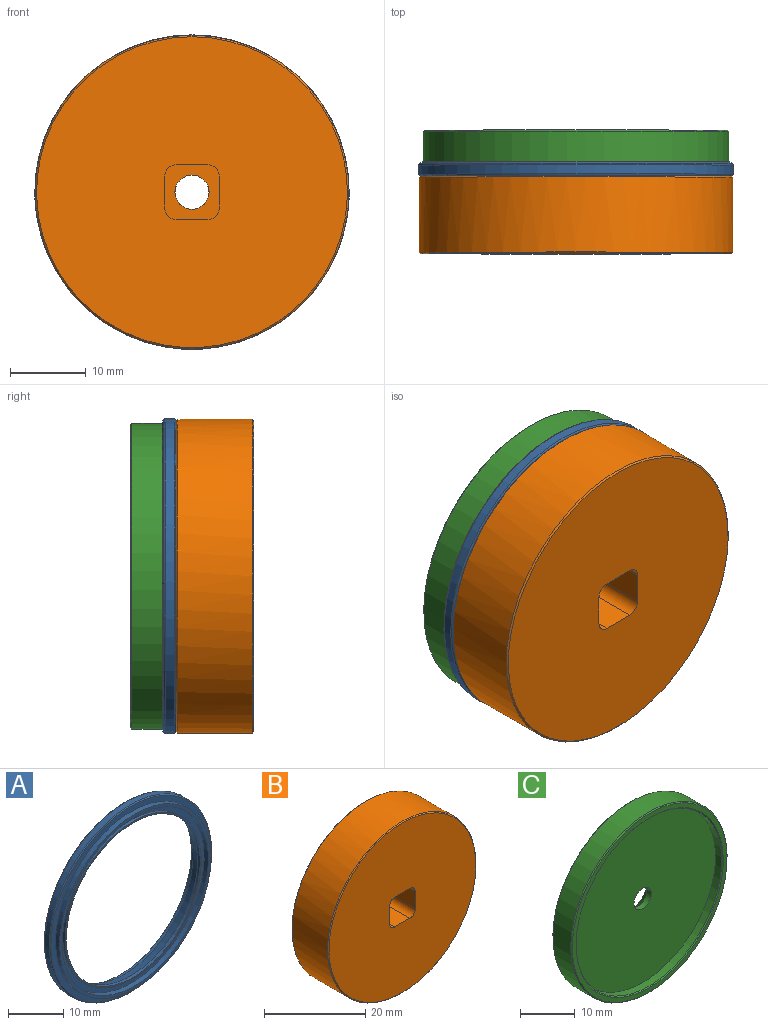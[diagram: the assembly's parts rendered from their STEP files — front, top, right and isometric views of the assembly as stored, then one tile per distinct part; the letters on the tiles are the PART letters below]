
ASSEMBLY  parts=3 mates=2
PART A: 22 faces, bbox 44.9x3.8x44.9 mm
  f0: cylinder r=18.75mm len=37.5mm, axis (0,1,0), area 129.6mm2, adj f1,f21
  f1: plane 38.7x38.7mm, normal (0,-1,0), area 71.8mm2, adj f0,f2
  f2: cylinder r=19.35mm len=38.7mm, axis (0,1,0), area 127.7mm2, adj f1,f3
  f3: plane 41.1x41.1mm, normal (0,-1,0), area 150.4mm2, adj f2,f4
  f4: torus R=20.55mm, axis (0,1,0), area 40.8mm2, adj f3,f5
  f5: cylinder r=20.75mm len=41.5mm, axis (0,1,0), area 155.5mm2, adj f4,f6
  f6: torus R=20.55mm, axis (0,1,0), area 25.6mm2, adj f5,f7
  f7: cone r=20.3mm half-angle=56.3deg, axis (0,-1,0), area 55.4mm2, adj f6,f8
  f8: torus R=20.28mm, axis (0,1,0), area 13.7mm2, adj f7,f9
  f9: cylinder r=20.23mm len=40.45mm, axis (0,1,0), area 96.1mm2, adj f8,f10
  f10: plane 40.45x40.45mm, normal (0,1,0), area 180.6mm2, adj f9,f11
  f11: cylinder r=18.75mm len=37.5mm, axis (0,1,0), area 106mm2, adj f10,f12
  f12: cone r=18.29mm half-angle=28.6deg, axis (0,-1,0), area 112.6mm2, adj f11,f13
  f13: plane 36.57x36.57mm, normal (0,1,0), area 9.9mm2, adj f12,f14
  f14: cylinder r=18.2mm len=36.4mm, axis (0,1,0), area 97.2mm2, adj f13,f15
  f15: cone r=18.2mm half-angle=30deg, axis (0,-1,0), area 19.9mm2, adj f14,f16
  f16: plane 36.57x36.57mm, normal (0,1,0), area 71.9mm2, adj f15,f17
  f17: cone r=17.15mm half-angle=16.9deg, axis (0,1,0), area 188.5mm2, adj f16,f18
  f18: cylinder r=17.15mm len=34.3mm, axis (0,1,0), area 70mm2, adj f17,f19
  f19: plane 34.9x34.9mm, normal (0,-1,0), area 32.6mm2, adj f18,f20
  f20: cylinder r=17.45mm len=34.9mm, axis (0,1,0), area 65.8mm2, adj f19,f21
  f21: plane 37.5x37.5mm, normal (0,-1,0), area 147.8mm2, adj f0,f20
PART B: 19 faces, bbox 41.4x10.3x41.4 mm
  f0: plane 41x41mm, normal (0,-1,0), area 1270.3mm2, adj f8,f9,f10,f11,f12,f13,f14,f15
  f1: cylinder r=2.25mm len=4.5mm, axis (0,1,0), area 36.8mm2, adj f7,f16
  f2: cylinder r=20.7mm len=41.4mm, axis (0,-1,0), area 1287.6mm2, adj f17,f18
  f3: plane 41x41mm, normal (0,1,0), area 137.9mm2, adj f4,f18
  f4: cylinder r=19.4mm len=38.8mm, axis (0,-1,0), area 128mm2, adj f3,f5
  f5: plane 38.8x38.8mm, normal (0,1,0), area 80.8mm2, adj f4,f6
  f6: cylinder r=18.72mm len=37.45mm, axis (0,-1,0), area 41.2mm2, adj f5,f7
  f7: plane 37.45x37.45mm, normal (0,1,0), area 1085.6mm2, adj f1,f6
  f8: plane 7x4.2mm, normal (0,0,1), area 29.4mm2, adj f0,f9,f15,f16
  f9: cylinder r=1.5mm len=7mm, axis (0,-1,0), area 16.5mm2, adj f0,f8,f10,f16
  f10: plane 7x4.2mm, normal (-1,0,0), area 29.4mm2, adj f0,f9,f11,f16
  f11: cylinder r=1.5mm len=7mm, axis (0,-1,0), area 16.5mm2, adj f0,f10,f12,f16
  f12: plane 7x4.2mm, normal (0,0,-1), area 29.4mm2, adj f0,f11,f13,f16
  f13: cylinder r=1.5mm len=7mm, axis (0,-1,0), area 16.5mm2, adj f0,f12,f14,f16
  f14: plane 7x4.2mm, normal (1,0,0), area 29.4mm2, adj f0,f13,f15,f16
  f15: cylinder r=1.5mm len=7mm, axis (0,-1,0), area 16.5mm2, adj f0,f8,f14,f16
  f16: plane 7.2x7.2mm, normal (0,-1,0), area 34mm2, adj f1,f8,f9,f10,f11,f12,f13,f14
  f17: cone r=20.5mm half-angle=45deg, axis (0,1,0), area 36.6mm2, adj f0,f2
  f18: cone r=20.7mm half-angle=45deg, axis (0,-1,0), area 36.6mm2, adj f2,f3
PART C: 10 faces, bbox 40.4x5x40.4 mm
  f0: plane 37.6x37.6mm, normal (0,-1,0), area 1094.5mm2, adj f1,f7
  f1: cylinder r=18.8mm len=37.6mm, axis (0,-1,0), area 189.6mm2, adj f0,f6
  f2: plane 39.95x39.95mm, normal (0,-1,0), area 119.4mm2, adj f5,f6
  f3: cylinder r=20.17mm len=40.35mm, axis (0,-1,0), area 583.1mm2, adj f5,f9
  f4: plane 39.95x39.95mm, normal (0,1,0), area 1196.8mm2, adj f8,f9
  f5: cone r=19.98mm half-angle=45deg, axis (0,1,0), area 35.7mm2, adj f2,f3
  f6: cone r=18.8mm half-angle=45deg, axis (0,-1,0), area 33.6mm2, adj f1,f2
  f7: cylinder r=2.25mm len=4.5mm, axis (0,1,0), area 16.9mm2, adj f0,f8
  f8: cone r=2.25mm half-angle=45deg, axis (0,1,0), area 57.8mm2, adj f4,f7
  f9: cone r=20.17mm half-angle=45deg, axis (0,-1,0), area 35.7mm2, adj f3,f4
PLACE A t=(-10.54,-10.66,4.21)mm
PLACE B t=(-8.34,-11.66,4.21)mm fixed
PLACE C t=(-8.89,-10.66,4.21)mm
MATE fastened A.f0 <-> C.f7  axis (0,1,0) through (-27.69,-10.66,4.21)mm
MATE fastened B.f1 <-> A.f0  axis (0,1,0) through (-27.69,-11.66,4.21)mm
